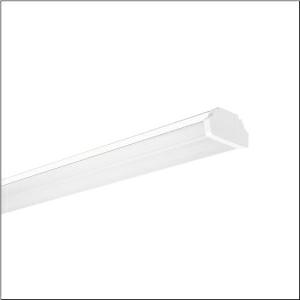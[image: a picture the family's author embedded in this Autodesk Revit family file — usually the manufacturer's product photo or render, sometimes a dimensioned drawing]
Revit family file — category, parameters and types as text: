
# Revit family: dus_31_gen_2_53bd812cv4dxd2_5f47
name_source: partatom
category: Lighting Fixtures
units: mm (PartAtom-declared; Revit-internal decimal feet)

## family parameters
Cut with Voids When Loaded = No
Host = Face
Light Source = No
Part Type = Normal
Room Calculation Point = No
Round Connector Dimension = Use Diameter
Shared = No

## types (1)
- --- (1 x LED, 13040 lm, 68.5 W, 4000K)
    Apparent Load = 69 VA
    CIE Flux Codes = 47 80 95 93 100
    Color Rendering = 80
    Color Temperature = 4000K
    Default Elevation = 1800 mm
    Description = DUS 31 Gen.2, luminaire insert, of sheet steel, coil coated, white, length: 1.535mm, width: 81mm, height: 90mm, 5x system unit, system units: 307mm, LED rated luminous flux: 13.040lm, light colour: 840, SDCM (Standard Deviation of Colour Matching)MacAdam ≤ 3 SDCM (initial), control gear: ON/OFF Multilumen, CLOi, with plug, 3-pole, with phase selection, mains connection: 220..240V, AC, 50/60Hz, start of lifetime: 69W, end of service life: 82W, through-wiring accessed according to module size, primary optical cover: cover, of PMMA, light emission: direct distribution, primary light characteristic: symmetric, protection rating (complete): IP20, protection rating (LED compartment): IP50, insulation class (complete): insulation class I (protective earthing), certification: CE, ENEC, VDE, UKCA, impact resistance: IK03, permissible ambient temperature for indoor applications: -35..+35°C, corresponds to IFS (International Featured Standards) requirements for safety and quality in the food industry, reducing of maximum allowable ambient temperature of 5°C with ceiling mounting, packaging unit: 1 piece
    Height = 95 mm
    Lamp = 1 x LED
    Lamp Light Flux = 13040 lm
    Lamp Power = 68.5 W
    Lamp count = 1
    Length = 1535 mm
    Luminous efficacy = 190 lm/W
    Manufacturer = Siteco
    ModVariant = No
    Model = 53BD812CV4DXD2
    Mounting Place = Ceiling
    Mounting Type = Pendant
    Number of Poles = 1
    OnlyDefault = Yes
    Power Factor = 1
    Product Name = DUS 31 Gen.2
    Product group = luminaire insert | ceiling pendant
    ProductGroupID = 901
    Protection Class = Protection class I
    Protection Degree = IP 20
    RLX_Detail_Level = 1
    RLX_Emergency_Light_Flux = 0 lm
    RLX_Emergency_Type = 0
    RLX_Emergency_Type_DB = No
    RlxData = <blob elided: 29997 chars, md5=f0900df1>
    Socket = socket
    Standby Power = 0 W
    System Light Flux = 13040 lm
    System Power = 69 W
    Type Comments = factory setting: luminous flux: 100 % | (A | C | E) | 161 mA
    Type Image = l_1319596.jpg
    URL = http://relux.com
    VarID = @adj_051221
    Voltage = 0 V
    Weight = 0.00 kg
    Width = 81 mm

## geometry (parser evidence)
native form markers: Blend x4, Sweep x12
no freeform markers — native parametric forms only
